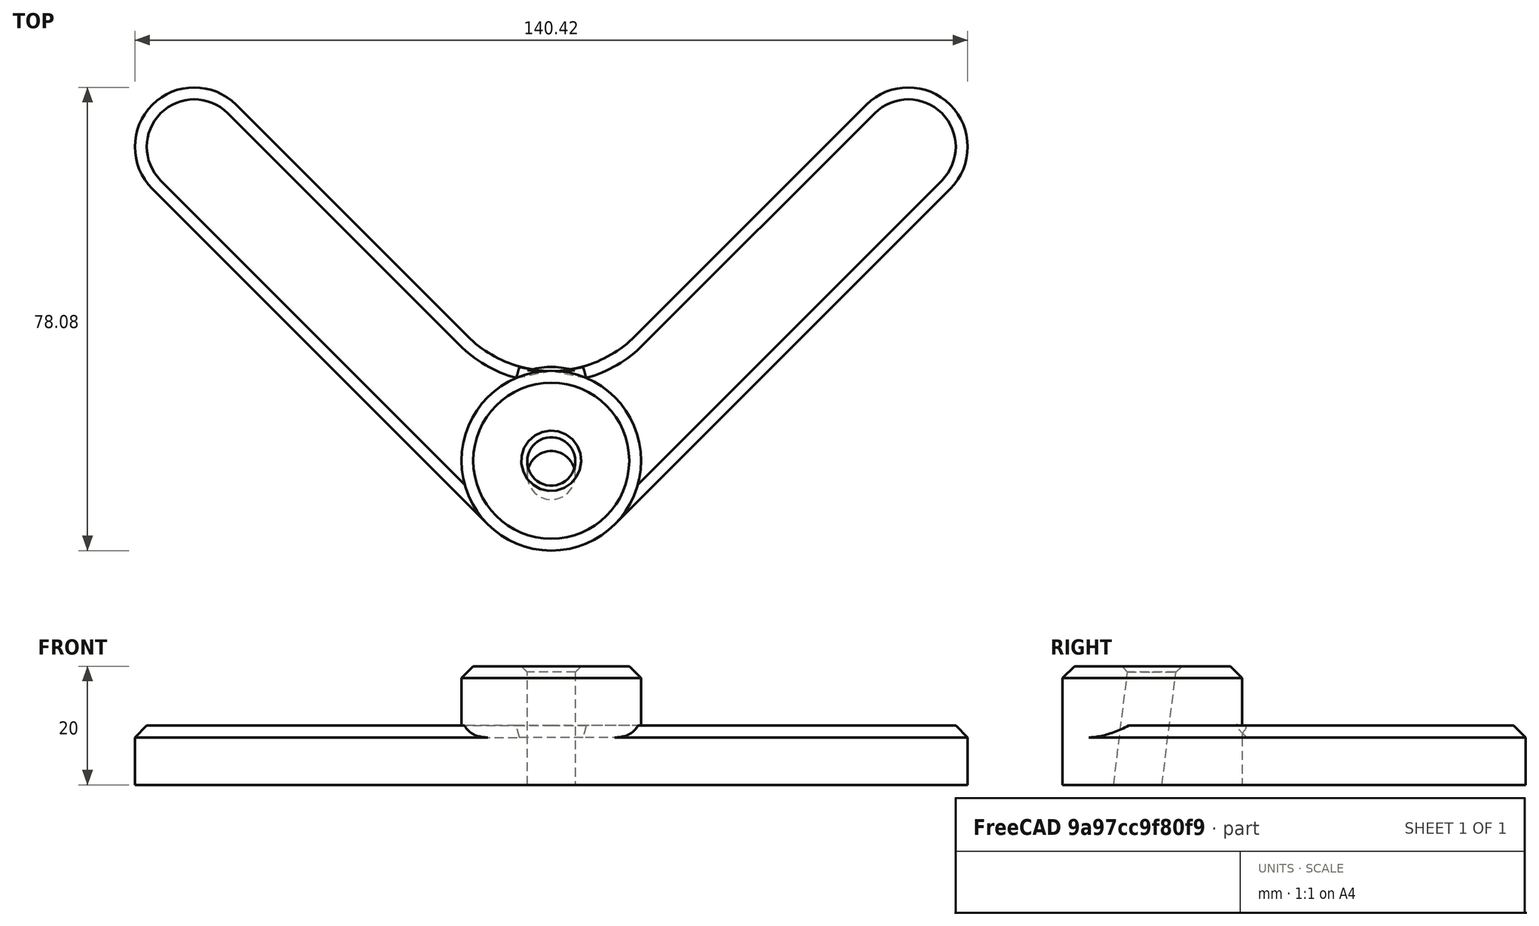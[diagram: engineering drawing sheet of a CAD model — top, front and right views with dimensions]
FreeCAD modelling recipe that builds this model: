
FCSTD DOCUMENT  (FreeCAD 0.19R22262 (Git))
Label: handyhalter_v2
License: All rights reserved
LicenseURL: http://en.wikipedia.org/wiki/All_rights_reserved
objects: Sketcher::SketchObject×4, PartDesign::Chamfer×3, PartDesign::Pad×2, PartDesign::Plane×1, PartDesign::Pocket×1, PartDesign::Body×1
note: 18 computed .brp shape members not serialized (recipe doc carries the construction recipe); baked Part::Feature solids carry a one-line shape summary decoded from their .brp

FEATURE [Sketcher::SketchObject] Sketch
  MapMode = 5
  Support = -> [XY_Plane]
  sketch-geometry (21):
    g0: LineSegment StartX=-67.2792 StartY=45.8579 StartZ=0 EndX=-10.7107 EndY=-10.7107 EndZ=0
    g1: ArcOfCircle CenterX=0 CenterY=0 CenterZ=0 NormalX=0 NormalY=0 NormalZ=1 AngleXU=0 Radius=15.1472 StartAngle=3.92699 EndAngle=5.49779
    g2: LineSegment StartX=10.7107 StartY=-10.7107 StartZ=0 EndX=67.2792 EndY=45.8579 EndZ=0
    g3: ArcOfCircle CenterX=60.2082 CenterY=52.9289 CenterZ=0 NormalX=0 NormalY=0 NormalZ=1 AngleXU=0 Radius=10 StartAngle=5.49779 EndAngle=8.63938
    g4: LineSegment StartX=53.1371 StartY=60 StartZ=0 EndX=14.1421 EndY=21.0051 EndZ=0
    g5: ArcOfCircle CenterX=0 CenterY=35.1472 CenterZ=0 NormalX=0 NormalY=0 NormalZ=1 AngleXU=0 Radius=20 StartAngle=3.92699 EndAngle=5.49779
    g6: LineSegment StartX=-14.1421 StartY=21.0051 StartZ=0 EndX=-53.1371 EndY=60 EndZ=0
    g7: ArcOfCircle CenterX=-60.2082 CenterY=52.9289 CenterZ=0 NormalX=0 NormalY=0 NormalZ=1 AngleXU=0 Radius=10 StartAngle=0.785398 EndAngle=3.92699
    g8: LineSegment [constr] StartX=53.1371 StartY=60 StartZ=0 EndX=67.2792 EndY=45.8579 EndZ=0
    g9: LineSegment [constr] StartX=-53.1371 StartY=60 StartZ=0 EndX=-67.2792 EndY=45.8579 EndZ=0
    g10: GeomPoint X=-1.78e-14 Y=15.1472 Z=0
    g11: GeomPoint X=0 Y=-15.1472 Z=0
    g12: LineSegment [constr] StartX=-10.7107 StartY=-10.7107 StartZ=0 EndX=10.7107 EndY=-10.7107 EndZ=0
    g13: LineSegment [constr] StartX=10.7107 StartY=-10.7107 StartZ=0 EndX=0 EndY=-15.1472 EndZ=0
    g14: LineSegment [constr] StartX=0 StartY=-15.1472 StartZ=0 EndX=-10.7107 EndY=-10.7107 EndZ=0
    g15: LineSegment [constr] StartX=14.1421 StartY=21.0051 StartZ=0 EndX=-1.78e-14 EndY=15.1472 EndZ=0
    g16: LineSegment [constr] StartX=-1.78e-14 StartY=15.1472 StartZ=0 EndX=-14.1421 EndY=21.0051 EndZ=0
    g17: LineSegment [constr] StartX=-14.1421 StartY=21.0051 StartZ=0 EndX=14.1421 EndY=21.0051 EndZ=0
    g18: GeomPoint X=0 Y=0 Z=0
    g19: LineSegment [constr] StartX=-1.78e-14 StartY=15.1472 StartZ=0 EndX=0 EndY=0 EndZ=0
    g20: LineSegment [constr] StartX=0 StartY=-15.1472 StartZ=0 EndX=0 EndY=0 EndZ=0
  constraints (48):
    c: Tangent(g0,g1) = -1.5708
    c: Coincident(g1,g2)
    c: Tangent(g2,g3) = -1.5708
    c: Coincident(g3,g4)
    c: Tangent(g4,g5) = 1.5708
    c: Coincident(g5,g6)
    c: Tangent(g6,g7) = -1.5708
    c: Coincident(g7,g0)
    c: Perpendicular(g4,g6)
    c: Equal(g0,g2)
    c: Equal(g6,g4)
    c: PointOnObject(g5,g-2)
    c: Coincident(g8,g3)
    c: Coincident(g8,g2)
    c: Coincident(g9,g6)
    c: Coincident(g9,g0)
    c: Equal(g9,g8)
    c: PointOnObject(g7,g9)
    c: PointOnObject(g3,g8)
    c: Parallel(g0,g6)
    c: Parallel(g4,g2)
    c: Distance(g8) = 20
    c: PointOnObject(g10,g5)
    c: PointOnObject(g11,g1)
    c: Coincident(g0,g12)
    c: Coincident(g12,g1)
    c: Horizontal(g12)
    c: Coincident(g12,g13)
    c: Coincident(g13,g11)
    c: Coincident(g13,g14)
    c: Coincident(g14,g12)
    c: Coincident(g4,g15)
    c: Coincident(g15,g10)
    c: Coincident(g15,g16)
    c: Coincident(g16,g5)
    c: Coincident(g16,g17)
    c: Coincident(g17,g15)
    c: Equal(g15,g16)
    c: Coincident(g19,g10)
    c: Coincident(g19,g18)
    c: Coincident(g20,g11)
    c: Coincident(g20,g18)
    c: Vertical(g20)
    c: Equal(g20,g19)
    c: Coincident(g-1,g18)
    c: Coincident(g1,g18)
    c: Radius(g5) = 20
    c: Distance(g0) = 80
FEATURE [PartDesign::Pad] Pad
  Length = 10
  Length2 = 100
  Profile = -> Sketch
  Refine = true
  Type = 0
FEATURE [Sketcher::SketchObject] Sketch001
  ExternalGeometry = -> [Pad]
  MapMode = 5
  Placement = pos=(0,0,10) rot=(0,0,1;0rad)
  Support = -> [Pad]
  sketch-geometry (1):
    g0: Circle CenterX=0 CenterY=0 CenterZ=0 NormalX=0 NormalY=0 NormalZ=1 AngleXU=0 Radius=15.1472
  constraints (2):
    c: Coincident(g0,g-1)
    c: PointOnObject(g-3,g0)
FEATURE [PartDesign::Pad] Pad001
  BaseFeature = -> Pad
  Length = 10
  Length2 = 100
  Profile = -> Sketch001
  Refine = true
  Type = 0
FEATURE [Sketcher::SketchObject] Sketch002
  ExternalGeometry = -> [Pad001]
  MapMode = 5
  Placement = pos=(0,0,0) rot=(0.57735,0.57735,0.57735;2.0944rad)
  Support = -> [YZ_Plane]
  sketch-geometry (2):
    g0: LineSegment StartX=-2.45569 StartY=0 StartZ=0 EndX=40.1986 EndY=347.391 EndZ=0
    g1: GeomPoint X=0 Y=20 Z=0
  constraints (6):
    c: PointOnObject(g0,g-1)
    c: Distance(g0) = 350
    c: Angle(g-1,g0) = 1.44862
    c: PointOnObject(g1,g0)
    c: Horizontal(g-3,g1)
    c: Vertical(g1,g-1)
FEATURE [PartDesign::Plane] DatumPlane
  AttachmentOffset = pos=(0,0,-22) rot=(0,0,1;0rad)
  Length = 163.315
  MapMode = 7
  Placement = pos=(-4.8e-15,0.225434,21.836) rot=(1,0,0;3.01942rad)
  ResizeMode = 0
  Support = -> [Sketch002]
  Width = 116.266
FEATURE [Sketcher::SketchObject] Sketch003
  MapMode = 5
  Placement = pos=(-4.8e-15,0.225434,21.836) rot=(1,0,0;3.01942rad)
  Support = -> [DatumPlane]
  sketch-geometry (1):
    g0: Circle CenterX=0 CenterY=0 CenterZ=0 NormalX=0 NormalY=0 NormalZ=1 AngleXU=0 Radius=4.05
  constraints (3):
    c: Radius(g0) = 4.05
    c: PointOnObject(g0,g-2)
    c: PointOnObject(g0,g-1)
FEATURE [PartDesign::Pocket] Pocket
  BaseFeature = -> Pad001
  Length = 5
  Length2 = 100
  Profile = -> Sketch003
  Refine = true
  Reversed = true
  Type = 1
FEATURE [PartDesign::Chamfer] Chamfer
  Angle = 45
  Base = -> Pocket [Edge13]
  BaseFeature = -> Pocket
  ChamferType = 0
  FlipDirection = false
  Refine = true
  Size = 2
  Size2 = 8
  SupportTransform = false
FEATURE [PartDesign::Chamfer] Chamfer001
  Angle = 45
  Base = -> Chamfer [Edge12,Edge13,Edge14,Edge17,Edge11,Edge16,Edge15,Edge18]
  BaseFeature = -> Chamfer
  ChamferType = 0
  FlipDirection = false
  Refine = true
  Size = 2
  Size2 = 1
  SupportTransform = false
FEATURE [PartDesign::Chamfer] Chamfer002
  Angle = 45
  Base = -> Chamfer001 [Edge53]
  BaseFeature = -> Chamfer001
  ChamferType = 0
  FlipDirection = false
  Refine = true
  Size = 1
  Size2 = 1
  SupportTransform = false
FEATURE [PartDesign::Body] Body  label="base"
  Group = -> [Sketch,Pad,Sketch001,Pad001,Sketch002,DatumPlane,Sketch003,Pocket,Chamfer,Chamfer001,Chamfer002]
  Origin = -> Origin
  Tip = -> Chamfer002
